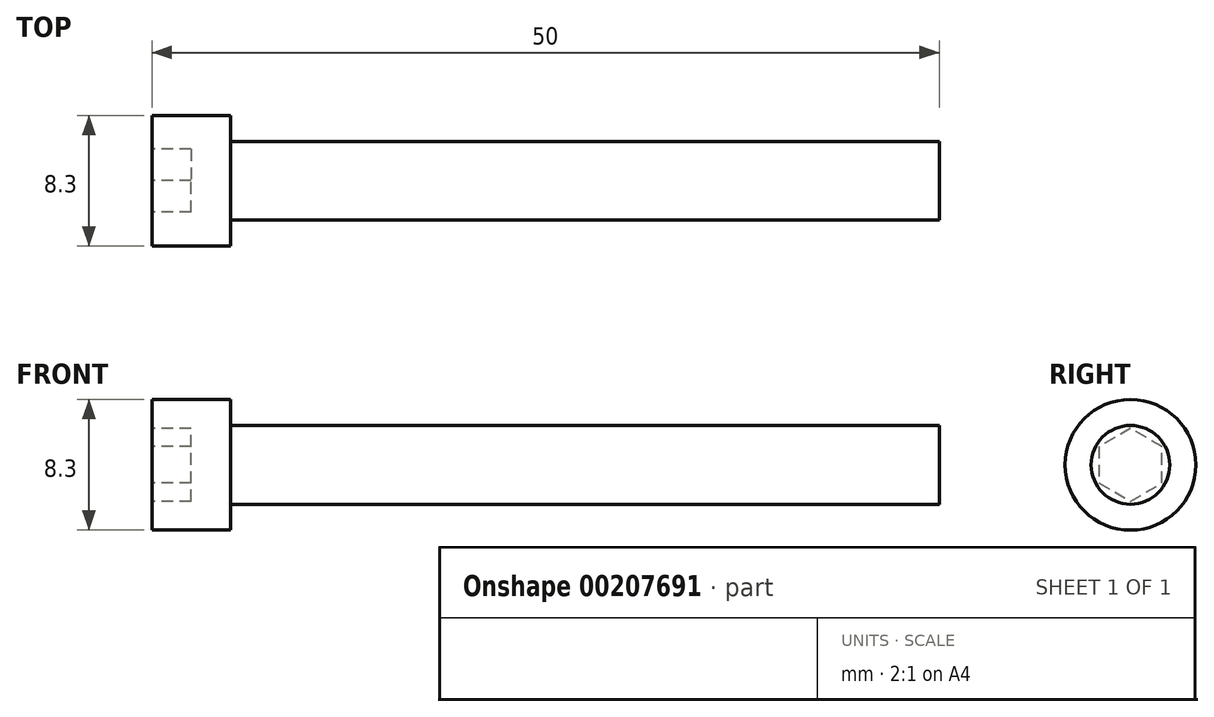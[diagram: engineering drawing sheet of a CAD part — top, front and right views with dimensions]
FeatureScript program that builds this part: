
annotation { "Feature Type Name" : "Feature", "Feature Type Description" : "" }
export const myFeature = defineFeature(function(context is Context, id is Id, definition is map)
    precondition{}
    {
        {
            var Q0;
            Q0=qCreatedBy(makeId("Front.planeOp"),FACE);
            var sketch = newSketch(context, id + "F0", { "sketchPlane" : qUnion([Q0])});
            skLineSegment(sketch, "E0.bottom", {"start": v(0, 2.5) * mm, "end": v(45, 2.5) * mm});
            skLineSegment(sketch, "E0.top", {"start": v(0, 0) * mm, "end": v(45, 0) * mm});
            skLineSegment(sketch, "E0.left", {"start": v(0, 2.5) * mm, "end": v(0, 0) * mm});
            skLineSegment(sketch, "E0.right", {"start": v(45, 2.5) * mm, "end": v(45, 0) * mm});
            skLineSegment(sketch, "E1.bottom", {"start": v(-5, 4.15) * mm, "end": v(0, 4.15) * mm});
            skLineSegment(sketch, "E1.top", {"start": v(-5, 0) * mm, "end": v(0, 0) * mm});
            skLineSegment(sketch, "E1.left", {"start": v(-5, 4.15) * mm, "end": v(-5, 0) * mm});
            skLineSegment(sketch, "E1.right", {"start": v(0, 4.15) * mm, "end": v(0, 0) * mm});
            skSolve(sketch);
        }
        {
            var Q0;
            Q0 = qSketchRegion(id + "F0", true);
            var Q1;
            Q1=sQuery(id+"F0.wireOp",EDGE,"E0.top");
            revolve(context, id + "F1", {"entities" : qUnion([Q0]), "axis" : qUnion([Q1]), "revolveType" : RevolveType.FULL});
        }
        {
            var Q0;
            Q0=makeQuery(id+"F1.opRevolve","SWEPT_FACE",FACE,{"disambiguationData":[OSD([sQuery(id+"F0.wireOp",EDGE,"E1.left")])]});
            var sketch = newSketch(context, id + "F2", { "sketchPlane" : qUnion([Q0])});
            skCircle(sketch, "E2.cCircle", {"center": v(0, 0) * mm, "radius": 2 * mm, "construction": true});
            skLineSegment(sketch, "E2.0", {"start": v(-2, 1.15) * mm, "end": v(0, 2.3) * mm});
            skLineSegment(sketch, "E2.1", {"start": v(0, 2.3) * mm, "end": v(2, 1.15) * mm});
            skLineSegment(sketch, "E2.2", {"start": v(2, 1.15) * mm, "end": v(2, -1.15) * mm});
            skLineSegment(sketch, "E2.3", {"start": v(2, -1.15) * mm, "end": v(0, -2.3) * mm});
            skLineSegment(sketch, "E2.4", {"start": v(0, -2.3) * mm, "end": v(-2, -1.15) * mm});
            skLineSegment(sketch, "E2.5", {"start": v(-2, -1.15) * mm, "end": v(-2, 1.15) * mm});
            skPoint(sketch, "E2.0.midPoint", {"position": v(-1, 1.73) * mm});
            skSolve(sketch);
        }
        {
            var Q0;
            Q0 = qSketchRegion(id + "F2", true);
            extrude(context, id + "F3", {"entities" : qUnion([Q0]), "operationType" : NewBodyOperationType.REMOVE, "oppositeDirection" : true, "depth" : 2.5 * mm});
        }
    });
